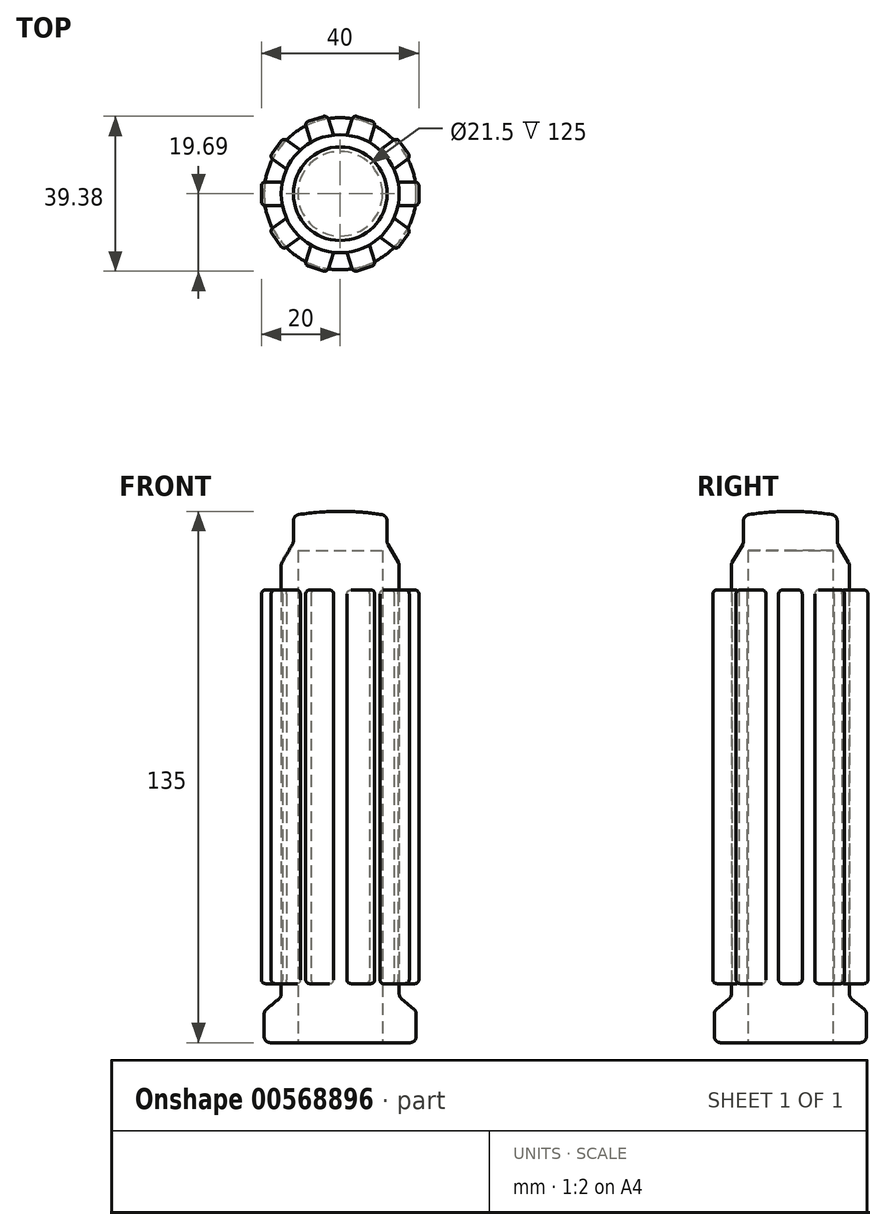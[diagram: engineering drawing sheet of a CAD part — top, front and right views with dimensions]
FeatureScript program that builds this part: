
annotation { "Feature Type Name" : "Feature", "Feature Type Description" : "" }
export const myFeature = defineFeature(function(context is Context, id is Id, definition is map)
    precondition{}
    {
        {
            var Q0;
            Q0=qCreatedBy(makeId("Front.planeOp"),FACE);
            var sketch = newSketch(context, id + "F0", { "sketchPlane" : qUnion([Q0])});
            skLineSegment(sketch, "E0", {"start": v(10.75, 0) * mm, "end": v(19.32, 0) * mm});
            skLineSegment(sketch, "E1", {"start": v(10.75, 0) * mm, "end": v(10.75, 125) * mm});
            skLineSegment(sketch, "E2", {"start": v(10.75, 125) * mm, "end": v(0, 125) * mm});
            skLineSegment(sketch, "E3", {"start": v(0, 125) * mm, "end": v(0, 135) * mm});
            skLineSegment(sketch, "E4", {"start": v(19.32, 0) * mm, "end": v(19.32, 8) * mm});
            skLineSegment(sketch, "E5", {"start": v(19.32, 8) * mm, "end": v(15, 11.63) * mm});
            skLineSegment(sketch, "E6", {"start": v(15, 11.63) * mm, "end": v(15, 121.63) * mm});
            skLineSegment(sketch, "E7", {"start": v(15, 121.63) * mm, "end": v(11.9, 127) * mm});
            skLineSegment(sketch, "E8", {"start": v(11.9, 127) * mm, "end": v(11.9, 133.95) * mm});
            skArc(sketch, "E9", {"start": v(11.9, 133.95) * mm, "mid": v(5.97, 134.74) * mm, "end": v(0, 135) * mm});
            skLineSegment(sketch, "E10", {"start": v(-19.32, 0) * mm, "end": v(19.32, 0) * mm});
            skLineSegment(sketch, "E11", {"start": v(0, 0) * mm, "end": v(0, 135) * mm, "construction": true});
            skSolve(sketch);
        }
        {
            var Q0;
            Q0 = qSketchRegion(id + "F0", true);
            var Q1;
            Q1=sQuery(id+"F0.wireOp",EDGE,"E11");
            revolve(context, id + "F1", {"entities" : qUnion([Q0]), "axis" : qUnion([Q1]), "revolveType" : RevolveType.FULL});
        }
        {
            var Q0;
            Q0=makeQuery(id+"F1.opRevolve","SWEPT_FACE",FACE,{"disambiguationData":[OSD([sQuery(id+"F0.wireOp",EDGE,"E4")])]});
            var Q1;
            Q1=makeQuery(id+"F1.opRevolve","SWEPT_EDGE",EDGE,{"disambiguationData":[OSD([sQuery(id+"F0.wireOp",EDGE,"E5"),sQuery(id+"F0.wireOp",EDGE,"E6")])]});
            var Q2;
            Q2=makeQuery(id+"F1.opRevolve","SWEPT_EDGE",EDGE,{"disambiguationData":[OSD([sQuery(id+"F0.wireOp",EDGE,"E6"),sQuery(id+"F0.wireOp",EDGE,"E7")])]});
            var Q3;
            Q3=makeQuery(id+"F1.opRevolve","SWEPT_EDGE",EDGE,{"disambiguationData":[OSD([sQuery(id+"F0.wireOp",EDGE,"E7"),sQuery(id+"F0.wireOp",EDGE,"E8")])]});
            var Q4;
            Q4=makeQuery(id+"F1.opRevolve","SWEPT_EDGE",EDGE,{"disambiguationData":[OSD([sQuery(id+"F0.wireOp",EDGE,"E8"),sQuery(id+"F0.wireOp",EDGE,"E9")])]});
            fillet(context, id + "F2", {"entities" : qUnion([Q0, Q1, Q2, Q3, Q4]), "radius" : 1.6 * mm, "tangentPropagation" : true, "allowEdgeOverflow" : false});
        }
        {
            var Q0;
            Q0=qCreatedBy(makeId("Right.planeOp"),FACE);
            cPlane(context, id + "F3", {"entities" : qUnion([Q0]), "cplaneType" : CPlaneType.OFFSET, "offset" : 20 * mm, "width" : 150 * mm, "height" : 150 * mm});
        }
        {
            var Q0;
            Q0=qCreatedBy(id+"F3.planeOp",FACE);
            var sketch = newSketch(context, id + "F4", { "sketchPlane" : qUnion([Q0])});
            skLineSegment(sketch, "E12.bottom", {"start": v(-3, 15) * mm, "end": v(3, 15) * mm});
            skLineSegment(sketch, "E12.top", {"start": v(-3, 115) * mm, "end": v(3, 115) * mm});
            skLineSegment(sketch, "E12.left", {"start": v(-3, 15) * mm, "end": v(-3, 115) * mm});
            skLineSegment(sketch, "E12.right", {"start": v(3, 15) * mm, "end": v(3, 115) * mm});
            skSolve(sketch);
        }
        {
            var Q0;
            Q0 = qSketchRegion(id + "F4", true);
            var Q1;
            Q1=makeQuery(id+"F1.opRevolve","SWEPT_FACE",FACE,{"disambiguationData":[OSD([sQuery(id+"F0.wireOp",EDGE,"E6")])]});
            extrude(context, id + "F5", {"entities" : qUnion([Q0]), "endBound" : BoundingType.UP_TO_SURFACE, "oppositeDirection" : true, "depth" : 25 * mm, "endBoundEntityFace" : qUnion([Q1]), "offsetDistance" : 25 * mm});
        }
        {
            var Q0;
            Q0=makeQuery(id+"F5.opExtrude","SWEPT_EDGE",EDGE,{"disambiguationData":[OSD([sQuery(id+"F4.wireOp",EDGE,"E12.bottom"),sQuery(id+"F4.wireOp",EDGE,"E12.left")])]});
            var Q1;
            Q1=makeQuery(id+"F5.opExtrude","CAP_EDGE",EDGE,{"disambiguationData":[OSD([sQuery(id+"F4.wireOp",EDGE,"E12.bottom")])],"isStart":true});
            var Q2;
            Q2=makeQuery(id+"F5.opExtrude","SWEPT_EDGE",EDGE,{"disambiguationData":[OSD([sQuery(id+"F4.wireOp",EDGE,"E12.bottom"),sQuery(id+"F4.wireOp",EDGE,"E12.right")])]});
            var Q3;
            Q3=makeQuery(id+"F5.opExtrude","CAP_EDGE",EDGE,{"disambiguationData":[OSD([sQuery(id+"F4.wireOp",EDGE,"E12.right")])],"isStart":true});
            var Q4;
            Q4=makeQuery(id+"F5.opExtrude","CAP_EDGE",EDGE,{"disambiguationData":[OSD([sQuery(id+"F4.wireOp",EDGE,"E12.left")])],"isStart":true});
            var Q5;
            Q5=makeQuery(id+"F5.opExtrude","SWEPT_EDGE",EDGE,{"disambiguationData":[OSD([sQuery(id+"F4.wireOp",EDGE,"E12.top"),sQuery(id+"F4.wireOp",EDGE,"E12.left")])]});
            var Q6;
            Q6=makeQuery(id+"F5.opExtrude","CAP_EDGE",EDGE,{"disambiguationData":[OSD([sQuery(id+"F4.wireOp",EDGE,"E12.top")])],"isStart":true});
            var Q7;
            Q7=makeQuery(id+"F5.opExtrude","SWEPT_EDGE",EDGE,{"disambiguationData":[OSD([sQuery(id+"F4.wireOp",EDGE,"E12.top"),sQuery(id+"F4.wireOp",EDGE,"E12.right")])]});
            fillet(context, id + "F6", {"entities" : qUnion([Q0, Q1, Q2, Q3, Q4, Q5, Q6, Q7]), "radius" : 1 * mm, "tangentPropagation" : true, "allowEdgeOverflow" : false});
        }
        {
            var Q0;
            Q0=makeQuery(id+"F5.opExtrude","SWEPT_BODY",BODY,{"disambiguationData":[OSD([sQuery(id+"F4.wireOp",EDGE,"E12.bottom"),sQuery(id+"F4.wireOp",EDGE,"E12.top"),sQuery(id+"F4.wireOp",EDGE,"E12.left"),sQuery(id+"F4.wireOp",EDGE,"E12.right")])]});
            var Q1;
            Q1=sQuery(id+"F0.wireOp",EDGE,"E11");
            circularPattern(context, id + "F7", {"entities" : qUnion([Q0]), "axis" : qUnion([Q1]), "angle" : 360 * degree, "instanceCount" : 10, "equalSpace" : true});
        }
    });
